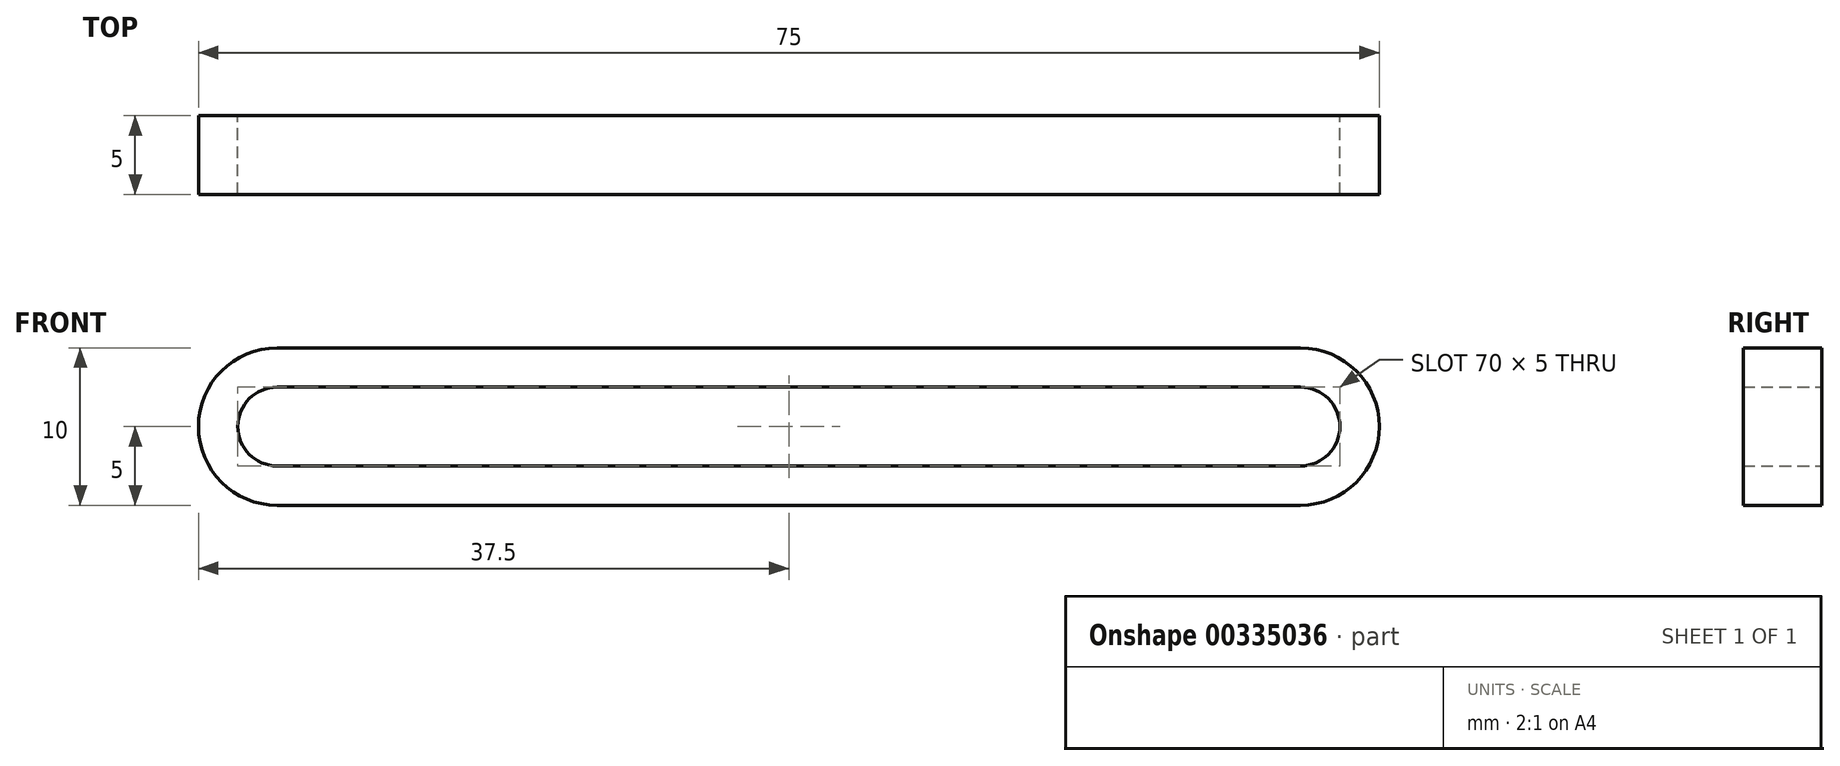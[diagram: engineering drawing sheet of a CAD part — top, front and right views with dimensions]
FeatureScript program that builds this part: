
annotation { "Feature Type Name" : "Feature", "Feature Type Description" : "" }
export const myFeature = defineFeature(function(context is Context, id is Id, definition is map)
    precondition{}
    {
        {
            var Q0;
            Q0=qCreatedBy(makeId("Front.planeOp"),FACE);
            var sketch = newSketch(context, id + "F0", { "sketchPlane" : qUnion([Q0])});
            skLineSegment(sketch, "E0.bottom", {"start": v(32.5, -5) * mm, "end": v(-32.5, -5) * mm});
            skLineSegment(sketch, "E0.top", {"start": v(32.5, 5) * mm, "end": v(-32.5, 5) * mm});
            skLineSegment(sketch, "E0.left", {"start": v(37.5, 0) * mm, "end": v(37.5, 0) * mm});
            skLineSegment(sketch, "E0.right", {"start": v(-37.5, 0) * mm, "end": v(-37.5, 0) * mm});
            skPoint(sketch, "E0.middle", {"position": v(0, 0) * mm});
            skPoint(sketch, "E1.visualSharp", {"position": v(-37.5, 5) * mm});
            skArc(sketch, "E1.filletArc", {"start": v(-32.5, 5) * mm, "mid": v(-36.04, 3.54) * mm, "end": v(-37.5, 0) * mm});
            skPoint(sketch, "E2.visualSharp", {"position": v(-37.5, -5) * mm});
            skArc(sketch, "E2.filletArc", {"start": v(-37.5, 0) * mm, "mid": v(-36.04, -3.54) * mm, "end": v(-32.5, -5) * mm});
            skPoint(sketch, "E3.visualSharp", {"position": v(37.5, -5) * mm});
            skArc(sketch, "E3.filletArc", {"start": v(32.5, -5) * mm, "mid": v(36.04, -3.54) * mm, "end": v(37.5, 0) * mm});
            skPoint(sketch, "E4.visualSharp", {"position": v(37.5, 5) * mm});
            skArc(sketch, "E4.filletArc", {"start": v(37.5, 0) * mm, "mid": v(36.04, 3.54) * mm, "end": v(32.5, 5) * mm});
            skSolve(sketch);
        }
        {
            var Q0;
            Q0 = qSketchRegion(id + "F0", true);
            extrude(context, id + "F1", {"entities" : qUnion([Q0]), "depth" : 5 * mm});
        }
        {
            var Q0;
            Q0=makeQuery(id+"F1.opExtrude","CAP_FACE",FACE,{"disambiguationData":[OSD([sQuery(id+"F0.wireOp",EDGE,"E0.bottom"),sQuery(id+"F0.wireOp",EDGE,"E0.top"),sQuery(id+"F0.wireOp",EDGE,"E1.filletArc"),sQuery(id+"F0.wireOp",EDGE,"E2.filletArc"),sQuery(id+"F0.wireOp",EDGE,"E3.filletArc"),sQuery(id+"F0.wireOp",EDGE,"E4.filletArc")])],"isStart":false});
            shell(context, id + "F2", {"entities" : qUnion([Q0]), "thickness" : 2.5 * mm});
        }
        {
            var Q0;
            Q0=makeQuery(id+"F2.opShell","OFFSET_FACE",FACE,{"disambiguationData":[OSD([sQuery(id+"F0.wireOp",EDGE,"E0.bottom"),sQuery(id+"F0.wireOp",EDGE,"E0.top"),sQuery(id+"F0.wireOp",EDGE,"E1.filletArc"),sQuery(id+"F0.wireOp",EDGE,"E2.filletArc"),sQuery(id+"F0.wireOp",EDGE,"E3.filletArc"),sQuery(id+"F0.wireOp",EDGE,"E4.filletArc")])]});
            extrude(context, id + "F3", {"entities" : qUnion([Q0]), "operationType" : NewBodyOperationType.REMOVE, "oppositeDirection" : true, "depth" : 25 * mm});
        }
    });
